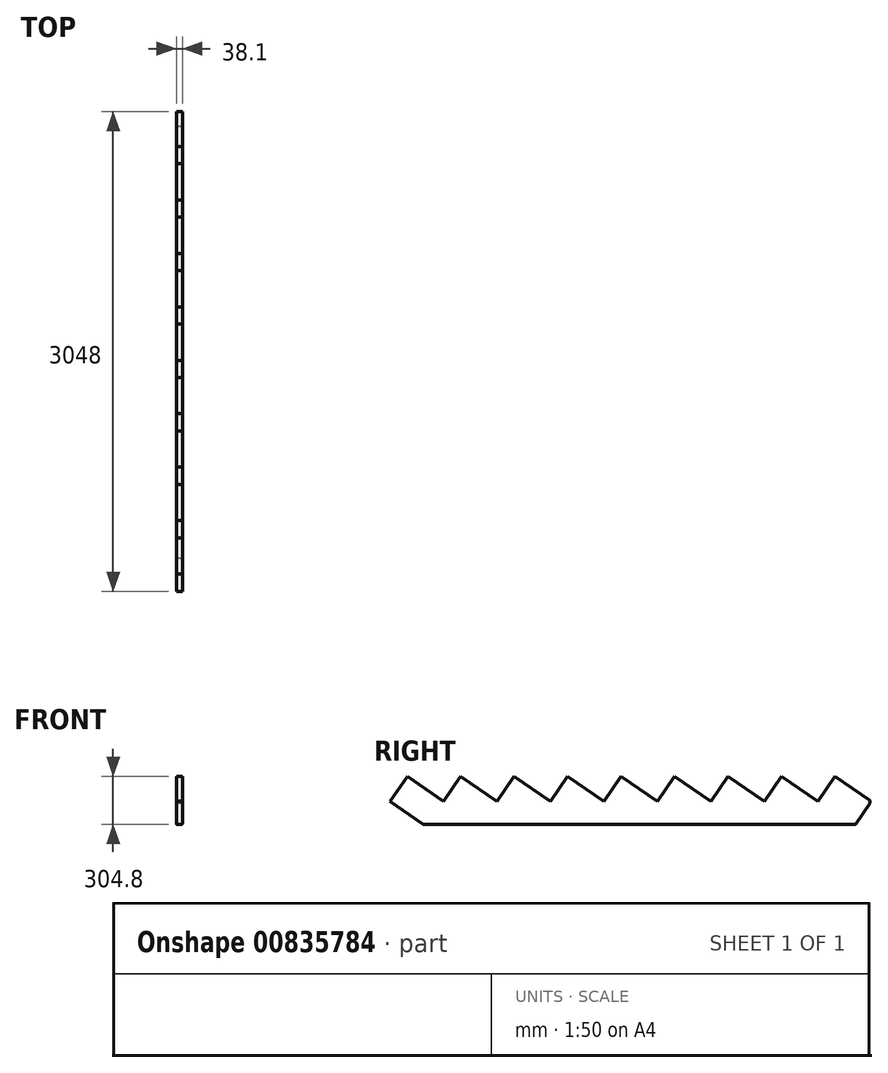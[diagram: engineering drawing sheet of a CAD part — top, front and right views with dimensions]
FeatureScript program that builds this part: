
annotation { "Feature Type Name" : "Feature", "Feature Type Description" : "" }
export const myFeature = defineFeature(function(context is Context, id is Id, definition is map)
    precondition{}
    {
        {
            var Q0;
            Q0=qCreatedBy(makeId("Front.planeOp"),FACE);
            var sketch = newSketch(context, id + "F0", { "sketchPlane" : qUnion([Q0])});
            skLineSegment(sketch, "E0.bottom", {"start": v(15.87, 171.45) * mm, "end": v(-15.88, 171.45) * mm});
            skLineSegment(sketch, "E0.top", {"start": v(15.88, -171.45) * mm, "end": v(-15.88, -171.45) * mm});
            skLineSegment(sketch, "E0.left", {"start": v(19.05, 168.28) * mm, "end": v(19.05, -168.28) * mm});
            skLineSegment(sketch, "E0.right", {"start": v(-19.05, 168.28) * mm, "end": v(-19.05, -168.28) * mm});
            skPoint(sketch, "E0.middle", {"position": v(0, 0) * mm});
            skPoint(sketch, "E1.visualSharp", {"position": v(-19.05, 171.45) * mm});
            skArc(sketch, "E1.filletArc", {"start": v(-15.88, 171.45) * mm, "mid": v(-18.12, 170.52) * mm, "end": v(-19.05, 168.28) * mm});
            skPoint(sketch, "E2.visualSharp", {"position": v(19.05, 171.45) * mm});
            skArc(sketch, "E2.filletArc", {"start": v(19.05, 168.28) * mm, "mid": v(18.12, 170.52) * mm, "end": v(15.87, 171.45) * mm});
            skPoint(sketch, "E3.visualSharp", {"position": v(19.05, -171.45) * mm});
            skArc(sketch, "E3.filletArc", {"start": v(15.88, -171.45) * mm, "mid": v(18.12, -170.52) * mm, "end": v(19.05, -168.28) * mm});
            skPoint(sketch, "E4.visualSharp", {"position": v(-19.05, -171.45) * mm});
            skArc(sketch, "E4.filletArc", {"start": v(-19.05, -168.28) * mm, "mid": v(-18.12, -170.52) * mm, "end": v(-15.88, -171.45) * mm});
            skSolve(sketch);
        }
        {
            var Q0;
            Q0=makeQuery(id+"F0.imprint","IMPRINT",FACE,{"disambiguationData":[TD([[makeQuery(id+"F0.imprint","IMPRINT",EDGE,{"derivedFrom":sQuery(id+"F0.wireOp",EDGE,"E0.bottom")}),1.0]])]});
            extrude(context, id + "F1", {"entities" : qUnion([Q0]), "endBound" : BoundingType.SYMMETRIC, "depth" : 3048 * mm, "offsetDistance" : 25.4 * mm});
        }
        {
            var Q0;
            Q0=makeQuery(id+"F1.opExtrude","SWEPT_FACE",FACE,{"disambiguationData":[OSD([sQuery(id+"F0.wireOp",EDGE,"E0.left")])]});
            var sketch = newSketch(context, id + "F2", { "sketchPlane" : qUnion([Q0])});
            skLineSegment(sketch, "E5", {"start": v(1532.52, -25.3) * mm, "end": v(1302.54, 133.35) * mm});
            skLineSegment(sketch, "E6", {"start": v(1302.54, 133.35) * mm, "end": v(1192.8, -25.47) * mm});
            skLineSegment(sketch, "E7", {"start": v(1192.8, -25.47) * mm, "end": v(962.94, 133.35) * mm});
            skLineSegment(sketch, "E8", {"start": v(962.94, 133.35) * mm, "end": v(853.2, -25.47) * mm});
            skLineSegment(sketch, "E9", {"start": v(853.2, -25.47) * mm, "end": v(623.34, 133.35) * mm});
            skLineSegment(sketch, "E10", {"start": v(623.34, 133.35) * mm, "end": v(513.6, -25.47) * mm});
            skLineSegment(sketch, "E11", {"start": v(513.6, -25.47) * mm, "end": v(283.73, 133.35) * mm});
            skLineSegment(sketch, "E12", {"start": v(283.73, 133.35) * mm, "end": v(174, -25.47) * mm});
            skLineSegment(sketch, "E13", {"start": v(174, -25.47) * mm, "end": v(-55.87, 133.35) * mm});
            skLineSegment(sketch, "E14", {"start": v(-55.87, 133.35) * mm, "end": v(-165.6, -25.47) * mm});
            skLineSegment(sketch, "E15", {"start": v(-165.6, -25.47) * mm, "end": v(-395.47, 133.35) * mm});
            skLineSegment(sketch, "E16", {"start": v(-395.47, 133.35) * mm, "end": v(-505.2, -25.47) * mm});
            skLineSegment(sketch, "E17", {"start": v(-505.2, -25.47) * mm, "end": v(-735.07, 133.35) * mm});
            skLineSegment(sketch, "E18", {"start": v(-735.07, 133.35) * mm, "end": v(-844.8, -25.47) * mm});
            skLineSegment(sketch, "E19", {"start": v(-844.8, -25.47) * mm, "end": v(-1074.67, 133.35) * mm});
            skLineSegment(sketch, "E20", {"start": v(-1074.67, 133.35) * mm, "end": v(-1184.4, -25.47) * mm});
            skLineSegment(sketch, "E21", {"start": v(-1184.4, -25.47) * mm, "end": v(-1414.27, 133.35) * mm});
            skLineSegment(sketch, "E22", {"start": v(-1414.27, 133.35) * mm, "end": v(-1524, -25.47) * mm});
            skLineSegment(sketch, "E23", {"start": v(-1524, -25.47) * mm, "end": v(-1312.71, -171.45) * mm});
            skLineSegment(sketch, "E24", {"start": v(1532.52, -25.3) * mm, "end": v(1431.65, -171.45) * mm});
            skLineSegment(sketch, "E25", {"start": v(-1312.71, -171.45) * mm, "end": v(-1716.17, -171.45) * mm});
            skLineSegment(sketch, "E26", {"start": v(-1716.17, -171.45) * mm, "end": v(-1716.17, 297.84) * mm});
            skLineSegment(sketch, "E27", {"start": v(-1716.17, 297.84) * mm, "end": v(1726.56, 297.84) * mm});
            skLineSegment(sketch, "E28", {"start": v(1726.56, 297.84) * mm, "end": v(1726.56, -171.45) * mm});
            skLineSegment(sketch, "E29", {"start": v(1726.56, -171.45) * mm, "end": v(1431.65, -171.45) * mm});
            skSolve(sketch);
        }
        {
            var Q0;
            Q0 = qSketchRegion(id + "F2", true);
            extrude(context, id + "F3", {"entities" : qUnion([Q0]), "operationType" : NewBodyOperationType.REMOVE, "endBound" : BoundingType.THROUGH_ALL, "oppositeDirection" : true, "depth" : 25.4 * mm, "offsetDistance" : 25.4 * mm});
        }
    });
